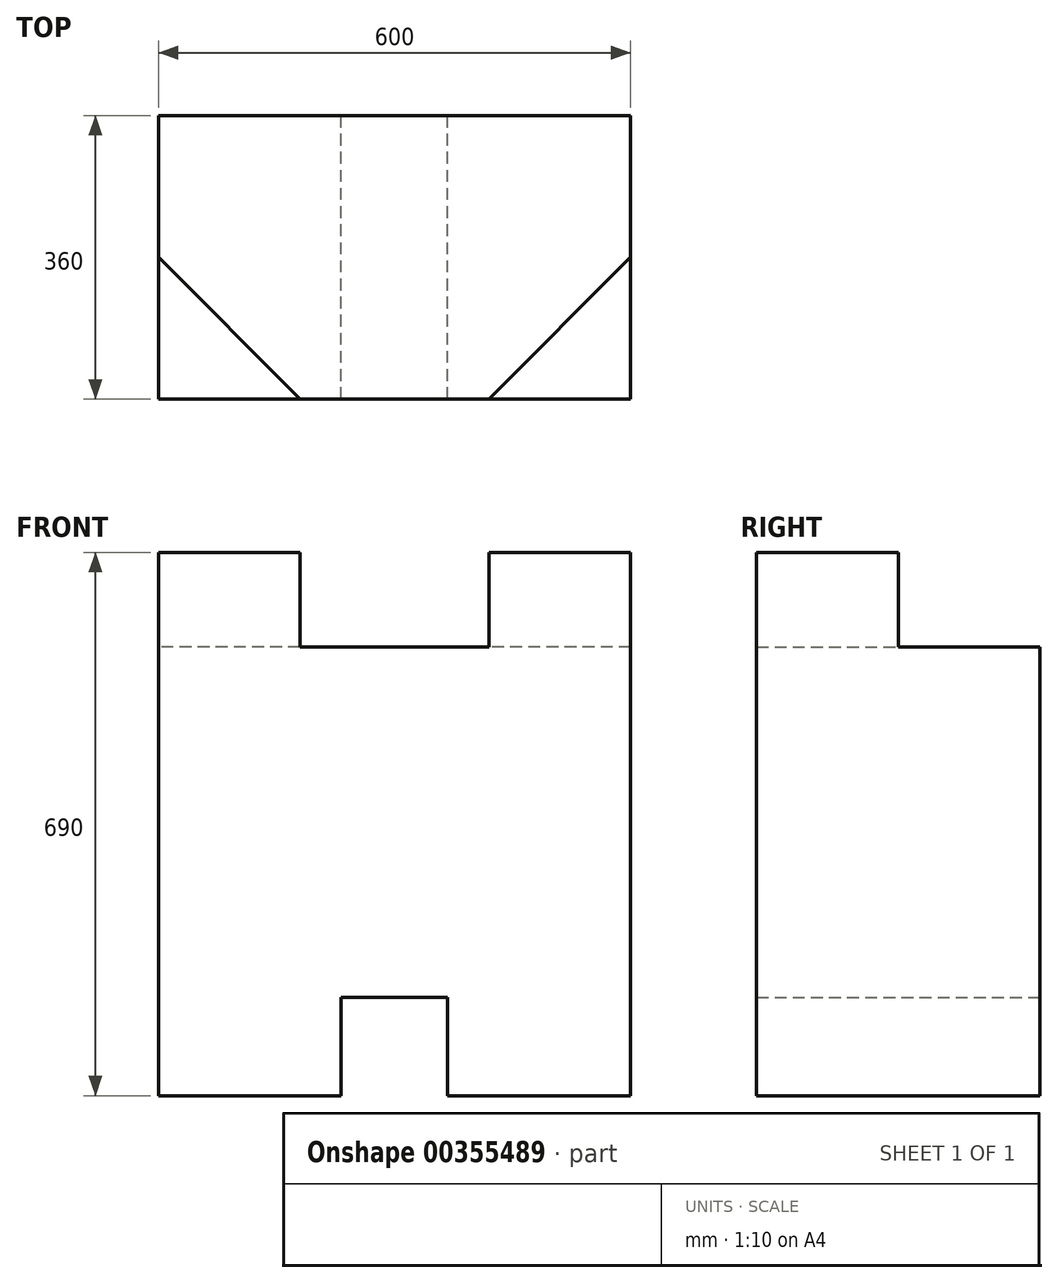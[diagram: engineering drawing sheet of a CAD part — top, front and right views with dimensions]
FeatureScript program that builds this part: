
annotation { "Feature Type Name" : "Feature", "Feature Type Description" : "" }
export const myFeature = defineFeature(function(context is Context, id is Id, definition is map)
    precondition{}
    {
        {
            var Q0;
            Q0=qCreatedBy(makeId("Front.planeOp"),FACE);
            var sketch = newSketch(context, id + "F0", { "sketchPlane" : qUnion([Q0])});
            skLineSegment(sketch, "E0.bottom", {"start": v(300, 285) * mm, "end": v(-300, 285) * mm});
            skLineSegment(sketch, "E0.top", {"start": v(300, -285) * mm, "end": v(67.6, -285) * mm});
            skLineSegment(sketch, "E0.left", {"start": v(300, 285) * mm, "end": v(300, -285) * mm});
            skLineSegment(sketch, "E0.right", {"start": v(-300, 285) * mm, "end": v(-300, -285) * mm});
            skPoint(sketch, "E0.middle", {"position": v(0, 0) * mm});
            skLineSegment(sketch, "E1.bottom", {"start": v(67.6, -160) * mm, "end": v(-67.6, -160) * mm});
            skLineSegment(sketch, "E1.left", {"start": v(67.6, -160) * mm, "end": v(67.6, -285) * mm});
            skLineSegment(sketch, "E1.right", {"start": v(-67.6, -160) * mm, "end": v(-67.6, -285) * mm});
            skPoint(sketch, "E1.middle", {"position": v(0, -285) * mm});
            skPoint(sketch, "E2.orphan", {"position": v(67.6, -410) * mm});
            skPoint(sketch, "E3.orphan", {"position": v(-67.6, -410) * mm});
            skLineSegment(sketch, "E4.trimOffspring", {"start": v(-67.6, -285) * mm, "end": v(-300, -285) * mm});
            skSolve(sketch);
        }
        {
            var Q0;
            Q0 = qSketchRegion(id + "F0", true);
            extrude(context, id + "F1", {"entities" : qUnion([Q0]), "depth" : 360 * mm});
        }
        {
            var Q0;
            Q0=makeQuery(id+"F1.opExtrude","SWEPT_FACE",FACE,{"disambiguationData":[OSD([sQuery(id+"F0.wireOp",EDGE,"E0.bottom")])]});
            var sketch = newSketch(context, id + "F2", { "sketchPlane" : qUnion([Q0])});
            skLineSegment(sketch, "E5", {"start": v(300, -360) * mm, "end": v(300, -180) * mm});
            skLineSegment(sketch, "E6", {"start": v(300, -180) * mm, "end": v(120, -360) * mm});
            skLineSegment(sketch, "E7", {"start": v(120, -360) * mm, "end": v(300, -360) * mm});
            skLineSegment(sketch, "E8", {"start": v(-300, -360) * mm, "end": v(-120, -360) * mm});
            skLineSegment(sketch, "E9", {"start": v(-120, -360) * mm, "end": v(-300, -180) * mm});
            skLineSegment(sketch, "E10", {"start": v(-300, -180) * mm, "end": v(-300, -360) * mm});
            skSolve(sketch);
        }
        {
            var Q0;
            Q0 = qSketchRegion(id + "F2", true);
            extrude(context, id + "F3", {"entities" : qUnion([Q0]), "operationType" : NewBodyOperationType.ADD, "depth" : 120 * mm});
        }
    });
